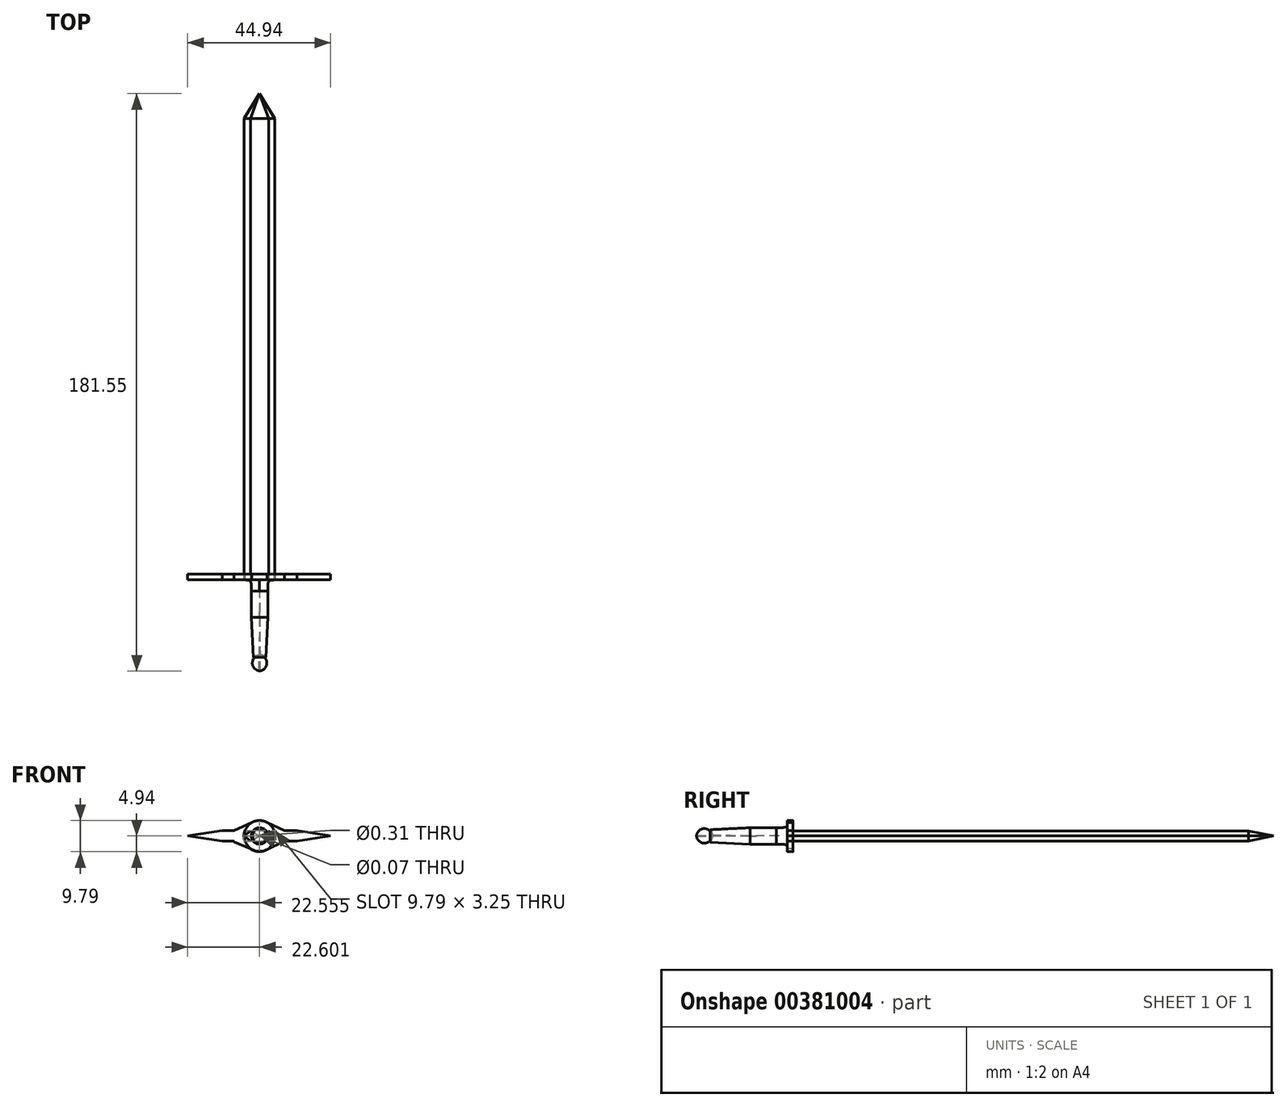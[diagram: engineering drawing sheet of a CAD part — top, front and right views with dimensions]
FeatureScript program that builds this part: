
annotation { "Feature Type Name" : "Feature", "Feature Type Description" : "" }
export const myFeature = defineFeature(function(context is Context, id is Id, definition is map)
    precondition{}
    {
        {
            var Q0;
            Q0=qCreatedBy(makeId("Top.planeOp"),FACE);
            var sketch = newSketch(context, id + "F0", { "sketchPlane" : qUnion([Q0])});
            skLineSegment(sketch, "E0", {"start": v(-127.1, -55.06) * mm, "end": v(-127.1, -61.54) * mm});
            skLineSegment(sketch, "E1", {"start": v(-127.7, -75.78) * mm, "end": v(-127.1, -63.23) * mm});
            skLineSegment(sketch, "E2", {"start": v(-124.83, -51.52) * mm, "end": v(-129.67, -51.52) * mm});
            skLineSegment(sketch, "E3", {"start": v(-129.67, -51.52) * mm, "end": v(-129.67, -54.16) * mm});
            skFitSpline(sketch, "E4", {"points": [v(-129.67, -54.16) * mm, v(-127.1, -55.06) * mm], "startDerivative": vector(4.15, -0.26) * mm, "endDerivative": vector(2.59, -2.32) * mm});
            skLineSegment(sketch, "E5", {"start": v(-127.1, -61.54) * mm, "end": v(-129.64, -61.54) * mm});
            skLineSegment(sketch, "E6", {"start": v(-129.64, -61.54) * mm, "end": v(-129.67, -54.16) * mm});
            skLineSegment(sketch, "E7", {"start": v(-129.64, -61.54) * mm, "end": v(-129.64, -63.25) * mm});
            skLineSegment(sketch, "E8", {"start": v(-129.64, -63.25) * mm, "end": v(-127.1, -63.23) * mm});
            skLineSegment(sketch, "E9", {"start": v(-129.64, -63.25) * mm, "end": v(-129.52, -75.1) * mm});
            skArc(sketch, "E10", {"start": v(-129.52, -75.1) * mm, "mid": v(-126.9, -77.63) * mm, "end": v(-129.52, -80.16) * mm});
            skLineSegment(sketch, "E11", {"start": v(-129.52, -75.1) * mm, "end": v(-129.52, -80.16) * mm});
            skLineSegment(sketch, "E12", {"start": v(-127.1, -61.54) * mm, "end": v(-127.1, -63.23) * mm});
            skFitSpline(sketch, "E13", {"points": [v(-127.1, -55.06) * mm, v(-124.83, -51.52) * mm], "startDerivative": vector(0.06, 10.63) * mm, "endDerivative": vector(6.8, 0) * mm});
            skSolve(sketch);
        }
        {
            var Q0;
            Q0=qSketchRegion(id+"F0",true);
            var Q1;
            Q1=sQuery(id+"F0.wireOp",EDGE,"E3");
            revolve(context, id + "F1", {"entities" : qUnion([Q0]), "axis" : qUnion([Q1]), "revolveType" : RevolveType.FULL});
        }
        {
            var Q0;
            {var subQ0=sQuery(id+"F0.wireOp",EDGE,"E2");Q0=makeQuery(id+"F1.opRevolve","SWEPT_FACE",FACE,{"disambiguationData":[OSD([subQ0]),TDD([makeQuery(id+"F0.imprint","IMPRINT",EDGE,{"disambiguationData":[TD([[makeQuery(id+"F0.imprint","INTERSECT",VERTEX,{"derivedFrom":[subQ0,sQuery(id+"F0.wireOp",EDGE,"E3")]}),1.0]])],"derivedFrom":subQ0})])]});}
            var sketch = newSketch(context, id + "F2", { "sketchPlane" : qUnion([Q0])});
            skLineSegment(sketch, "E14.bottom", {"start": v(141.43, 1.62) * mm, "end": v(117.91, 1.62) * mm});
            skLineSegment(sketch, "E14.top", {"start": v(141.43, -1.62) * mm, "end": v(117.91, -1.62) * mm});
            skLineSegment(sketch, "E14.left", {"start": v(141.43, 1.62) * mm, "end": v(141.43, -1.62) * mm});
            skLineSegment(sketch, "E14.right", {"start": v(117.91, 1.62) * mm, "end": v(117.91, -1.62) * mm});
            skPoint(sketch, "E14.middle", {"position": v(129.67, 0) * mm});
            skPoint(sketch, "E15.middle", {"position": v(129.67, 3.45) * mm});
            skPoint(sketch, "E16.middle", {"position": v(129.67, -1.62) * mm});
            skLineSegment(sketch, "E17", {"start": v(117.91, 1.62) * mm, "end": v(107.33, 0) * mm});
            skPoint(sketch, "E17.endSnap0", {"position": v(117.91, 0) * mm});
            skLineSegment(sketch, "E18", {"start": v(107.33, 0) * mm, "end": v(117.91, -1.62) * mm});
            skLineSegment(sketch, "E19", {"start": v(141.43, -1.62) * mm, "end": v(152.27, 0) * mm});
            skLineSegment(sketch, "E20", {"start": v(152.27, 0) * mm, "end": v(141.43, 1.62) * mm});
            skPoint(sketch, "E21", {"position": v(141.43, 0) * mm});
            skArc(sketch, "E22", {"start": v(125.1, 1.62) * mm, "mid": v(133.25, -3.43) * mm, "end": v(127.86, 4.49) * mm});
            skArc(sketch, "E23", {"start": v(127.86, 4.49) * mm, "mid": v(126.18, 3.35) * mm, "end": v(125.1, 1.62) * mm});
            skLineSegment(sketch, "E24", {"start": v(121.8, -1.62) * mm, "end": v(121.8, 1.62) * mm});
            skLineSegment(sketch, "E25", {"start": v(121.8, 1.62) * mm, "end": v(127.86, 4.49) * mm});
            skLineSegment(sketch, "E26", {"start": v(121.8, -1.62) * mm, "end": v(127.86, -4.59) * mm});
            skLineSegment(sketch, "E27", {"start": v(137.7, 1.62) * mm, "end": v(137.7, -1.91) * mm});
            skLineSegment(sketch, "E28", {"start": v(137.7, -1.91) * mm, "end": v(131.56, -4.46) * mm});
            skLineSegment(sketch, "E29", {"start": v(137.7, 1.62) * mm, "end": v(131.59, 4.47) * mm});
            skSolve(sketch);
        }
        {
            var Q0;
            Q0=qSketchRegion(id+"F2",true);
            extrude(context, id + "F3", {"entities" : qUnion([Q0]), "depth" : 1.78 * mm});
        }
        {
            var Q0;
            Q0=makeQuery(id+"F1.opRevolve","SWEPT_FACE",FACE,{"disambiguationData":[OSD([sQuery(id+"F0.wireOp",EDGE,"E2")])]});
            var sketch = newSketch(context, id + "F4", { "sketchPlane" : qUnion([Q0])});
            skLineSegment(sketch, "E30", {"start": v(124.83, 0) * mm, "end": v(126.83, 1.53) * mm});
            skLineSegment(sketch, "E31", {"start": v(124.83, 0) * mm, "end": v(126.83, -1.57) * mm});
            skLineSegment(sketch, "E32", {"start": v(134.5, 0) * mm, "end": v(132.53, 1.57) * mm});
            skLineSegment(sketch, "E33", {"start": v(134.5, 0) * mm, "end": v(132.56, -1.57) * mm});
            skLineSegment(sketch, "E34", {"start": v(132.56, -1.57) * mm, "end": v(126.83, -1.57) * mm});
            skLineSegment(sketch, "E35", {"start": v(126.83, 1.53) * mm, "end": v(132.53, 1.57) * mm});
            skSolve(sketch);
        }
        {
            var Q0;
            Q0=makeQuery(id+"F4.imprint","IMPRINT",FACE,{"disambiguationData":[TD([[makeQuery(id+"F4.imprint","IMPRINT",EDGE,{"derivedFrom":sQuery(id+"F4.wireOp",EDGE,"E30")}),-1.0]])]});
            extrude(context, id + "F5", {"entities" : qUnion([Q0]), "depth" : 145.03 * mm});
        }
        {
            var Q0;
            Q0=makeQuery(id+"F5.opExtrude","CAP_FACE",FACE,{"disambiguationData":[OSD([sQuery(id+"F4.wireOp",EDGE,"E30"),sQuery(id+"F4.wireOp",EDGE,"E31"),sQuery(id+"F4.wireOp",EDGE,"E32"),sQuery(id+"F4.wireOp",EDGE,"E33"),sQuery(id+"F4.wireOp",EDGE,"E34"),sQuery(id+"F4.wireOp",EDGE,"E35")])],"isStart":false});
            var sketch = newSketch(context, id + "F6", { "sketchPlane" : qUnion([Q0])});
            skPoint(sketch, "E36.positionSnap0", {"position": v(129.7, -1.57) * mm});
            skLineSegment(sketch, "E37", {"start": v(124.83, 0) * mm, "end": v(124.83, 0) * mm});
            skSolve(sketch);
        }
        {
            var Q0;
            {var subQ2=sQuery(id+"F6.wireOp",EDGE,"E37");Q0=makeQuery(id+"F6.imprint","IMPRINT",FACE,{"disambiguationData":[TD([[makeQuery(id+"F6.imprint","IMPRINT",EDGE,{"derivedFrom":subQ2}),-1.0]])]});}
            cPlane(context, id + "F7", {"entities" : qUnion([Q0]), "cplaneType" : CPlaneType.OFFSET, "offset" : 7.87 * mm, "width" : 152.4 * mm, "height" : 152.4 * mm});
        }
        {
            var Q0;
            Q0=qCreatedBy(id+"F7.planeOp",FACE);
            var sketch = newSketch(context, id + "F8", { "sketchPlane" : qUnion([Q0])});
            skCircle(sketch, "E38", {"center": v(129.7, 0) * mm, "radius": 0 * mm});
            skSolve(sketch);
        }
        {
            var Q1;
            {var subQ2=sQuery(id+"F6.wireOp",EDGE,"E37");Q1=makeQuery(id+"F6.imprint","IMPRINT",FACE,{"disambiguationData":[TD([[makeQuery(id+"F6.imprint","IMPRINT",EDGE,{"derivedFrom":subQ2}),-1.0]])]});}
            var Q2;
            Q2=sQuery(id+"F8.wireOp",VERTEX,"E38.center");
            loft(context, id + "F9", {"operationType" : NewBodyOperationType.ADD, "sheetProfilesArray" : [{ "sheetProfileEntities" : qUnion([Q1]) }, { "sheetProfileEntities" : qUnion([Q2]) }]});
        }
    });
